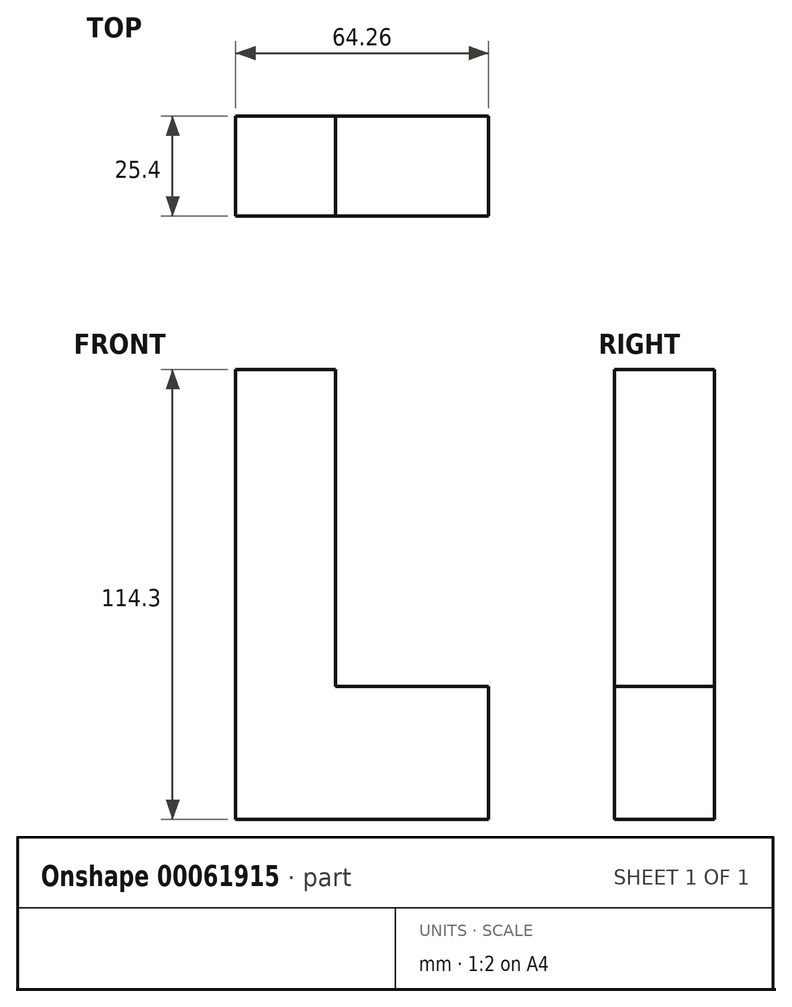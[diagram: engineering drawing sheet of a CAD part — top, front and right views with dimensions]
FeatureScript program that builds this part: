
annotation { "Feature Type Name" : "Feature", "Feature Type Description" : "" }
export const myFeature = defineFeature(function(context is Context, id is Id, definition is map)
    precondition{}
    {
        {
            var Q0;
            Q0=qCreatedBy(makeId("Front.planeOp"),FACE);
            var sketch = newSketch(context, id + "F0", { "sketchPlane" : qUnion([Q0])});
            skLineSegment(sketch, "E0.bottom", {"start": v(0, 0) * mm, "end": v(25.4, 0) * mm});
            skLineSegment(sketch, "E0.top", {"start": v(0, 114.3) * mm, "end": v(25.4, 114.3) * mm});
            skLineSegment(sketch, "E0.left", {"start": v(0, 0) * mm, "end": v(0, 114.3) * mm});
            skLineSegment(sketch, "E0.right", {"start": v(25.4, 0) * mm, "end": v(25.4, 114.3) * mm});
            skSolve(sketch);
        }
        {
            var Q0;
            Q0 = qSketchRegion(id + "F0", true);
            extrude(context, id + "F1", {"entities" : qUnion([Q0]), "depth" : 25.4 * mm});
        }
        {
            var Q0;
            Q0=makeQuery(id+"F1.opExtrude","CAP_FACE",FACE,{"disambiguationData":[OSD([sQuery(id+"F0.wireOp",EDGE,"E0.bottom"),sQuery(id+"F0.wireOp",EDGE,"E0.top"),sQuery(id+"F0.wireOp",EDGE,"E0.left"),sQuery(id+"F0.wireOp",EDGE,"E0.right")])],"isStart":false});
            var sketch = newSketch(context, id + "F2", { "sketchPlane" : qUnion([Q0])});
            skLineSegment(sketch, "E1.bottom", {"start": v(0, 0) * mm, "end": v(64.26, 0) * mm});
            skLineSegment(sketch, "E1.top", {"start": v(0, 33.83) * mm, "end": v(64.26, 33.83) * mm});
            skLineSegment(sketch, "E1.left", {"start": v(0, 0) * mm, "end": v(0, 33.83) * mm});
            skLineSegment(sketch, "E1.right", {"start": v(64.26, 0) * mm, "end": v(64.26, 33.83) * mm});
            skSolve(sketch);
        }
        {
            var Q0;
            Q0 = qSketchRegion(id + "F2", true);
            extrude(context, id + "F3", {"entities" : qUnion([Q0]), "operationType" : NewBodyOperationType.ADD, "oppositeDirection" : true, "depth" : 25.4 * mm});
        }
    });
